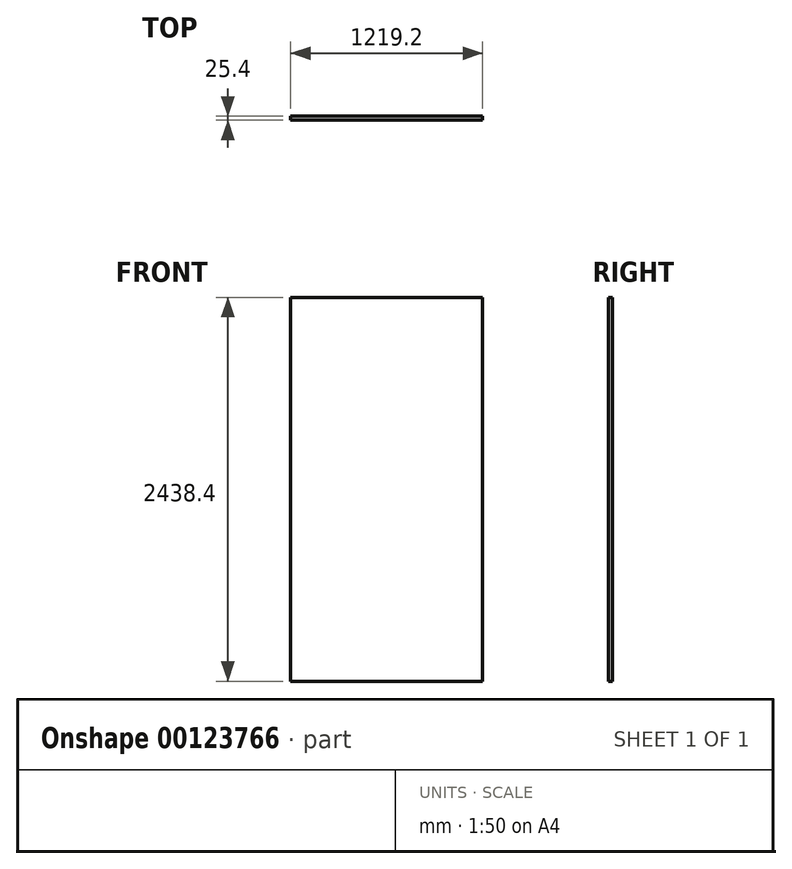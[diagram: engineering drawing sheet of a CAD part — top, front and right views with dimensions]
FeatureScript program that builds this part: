
annotation { "Feature Type Name" : "Feature", "Feature Type Description" : "" }
export const myFeature = defineFeature(function(context is Context, id is Id, definition is map)
    precondition{}
    {
        {
            var Q0;
            Q0=qCreatedBy(makeId("Front.planeOp"),FACE);
            var sketch = newSketch(context, id + "F0", { "sketchPlane" : qUnion([Q0])});
            skLineSegment(sketch, "E0.bottom", {"start": v(-619.1, 2126.35) * mm, "end": v(600.1, 2126.35) * mm});
            skLineSegment(sketch, "E0.top", {"start": v(-619.1, -312.05) * mm, "end": v(600.1, -312.05) * mm});
            skLineSegment(sketch, "E0.left", {"start": v(-619.1, 2126.35) * mm, "end": v(-619.1, -312.05) * mm});
            skLineSegment(sketch, "E0.right", {"start": v(600.1, 2126.35) * mm, "end": v(600.1, -312.05) * mm});
            skSolve(sketch);
        }
        {
            var Q0;
            Q0=makeQuery(id+"F0.imprint","IMPRINT",FACE,{"disambiguationData":[TD([[makeQuery(id+"F0.imprint","IMPRINT",EDGE,{"derivedFrom":sQuery(id+"F0.wireOp",EDGE,"E0.bottom")}),-1.0]])]});
            extrude(context, id + "F1", {"entities" : qUnion([Q0]), "depth" : 25.4 * mm});
        }
    });
